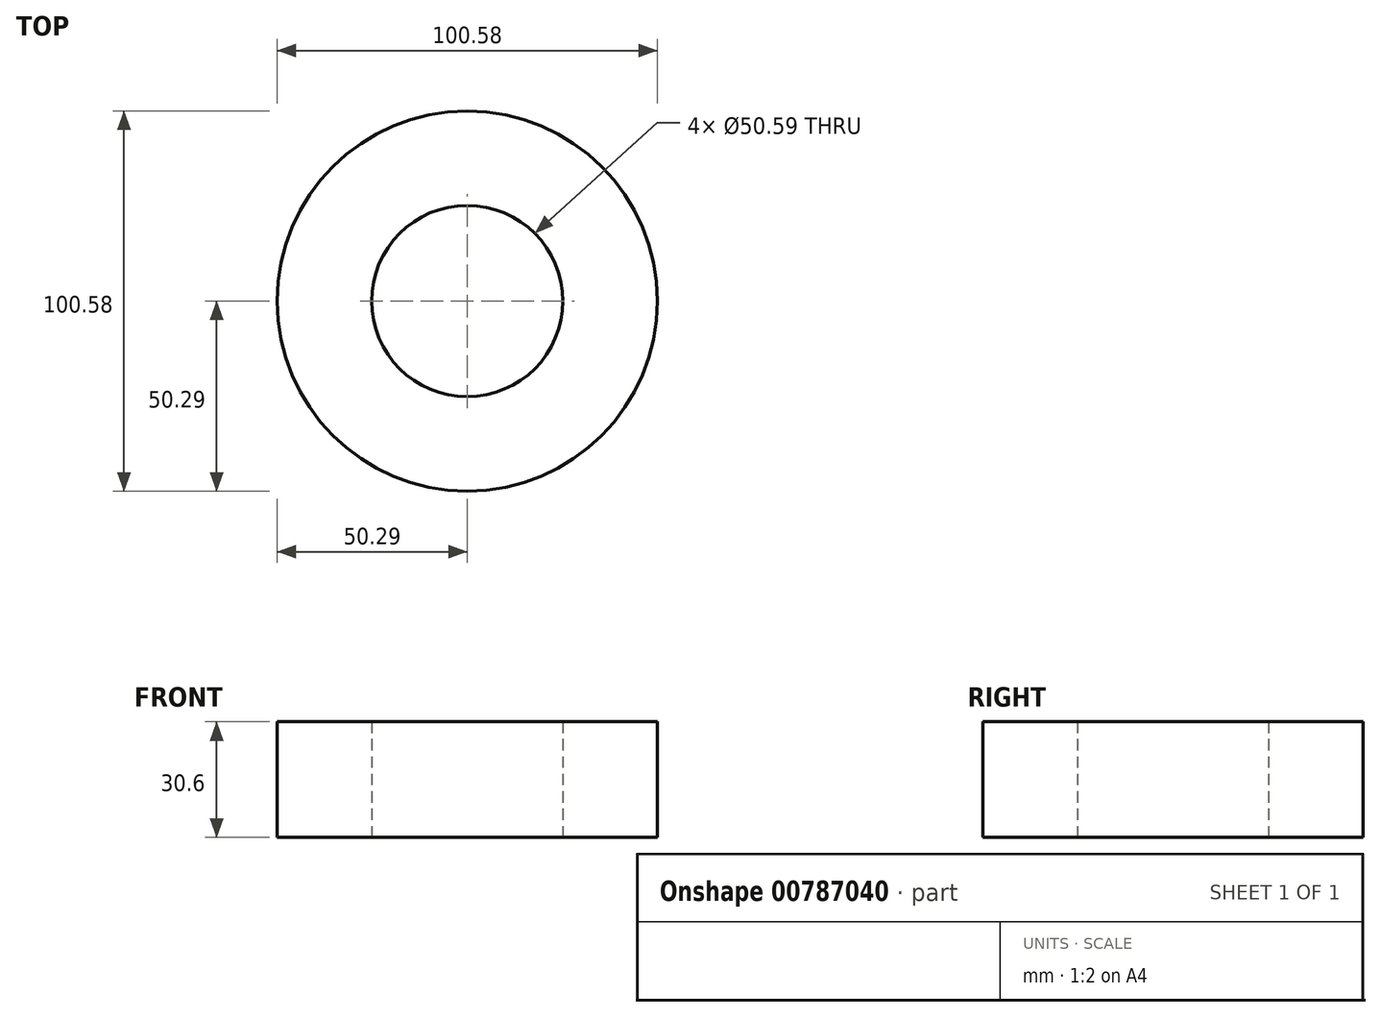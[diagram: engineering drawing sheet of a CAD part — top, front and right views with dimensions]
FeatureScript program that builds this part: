
annotation { "Feature Type Name" : "Feature", "Feature Type Description" : "" }
export const myFeature = defineFeature(function(context is Context, id is Id, definition is map)
    precondition{}
    {
        {
            var Q0;
            Q0=qCreatedBy(makeId("Top.planeOp"),FACE);
            var sketch = newSketch(context, id + "F0", { "sketchPlane" : qUnion([Q0])});
            skCircle(sketch, "E0", {"center": v(0, 0) * mm, "radius": 25.3 * mm});
            skCircle(sketch, "E1.0", {"center": v(0, 0) * mm, "radius": 50.5 * mm});
            skCircle(sketch, "E2.0", {"center": v(0, 0) * mm, "radius": 50.3 * mm});
            skSolve(sketch);
        }
        {
            var Q0;
            Q0=makeQuery(id+"F0.imprint","IMPRINT",FACE,{"disambiguationData":[TD([[makeQuery(id+"F0.imprint","IMPRINT",EDGE,{"derivedFrom":sQuery(id+"F0.wireOp",EDGE,"E0")}),-1.0]])]});
            extrude(context, id + "F1", {"entities" : qUnion([Q0]), "depth" : 30.6 * mm, "offsetDistance" : 25 * mm});
        }
    });
